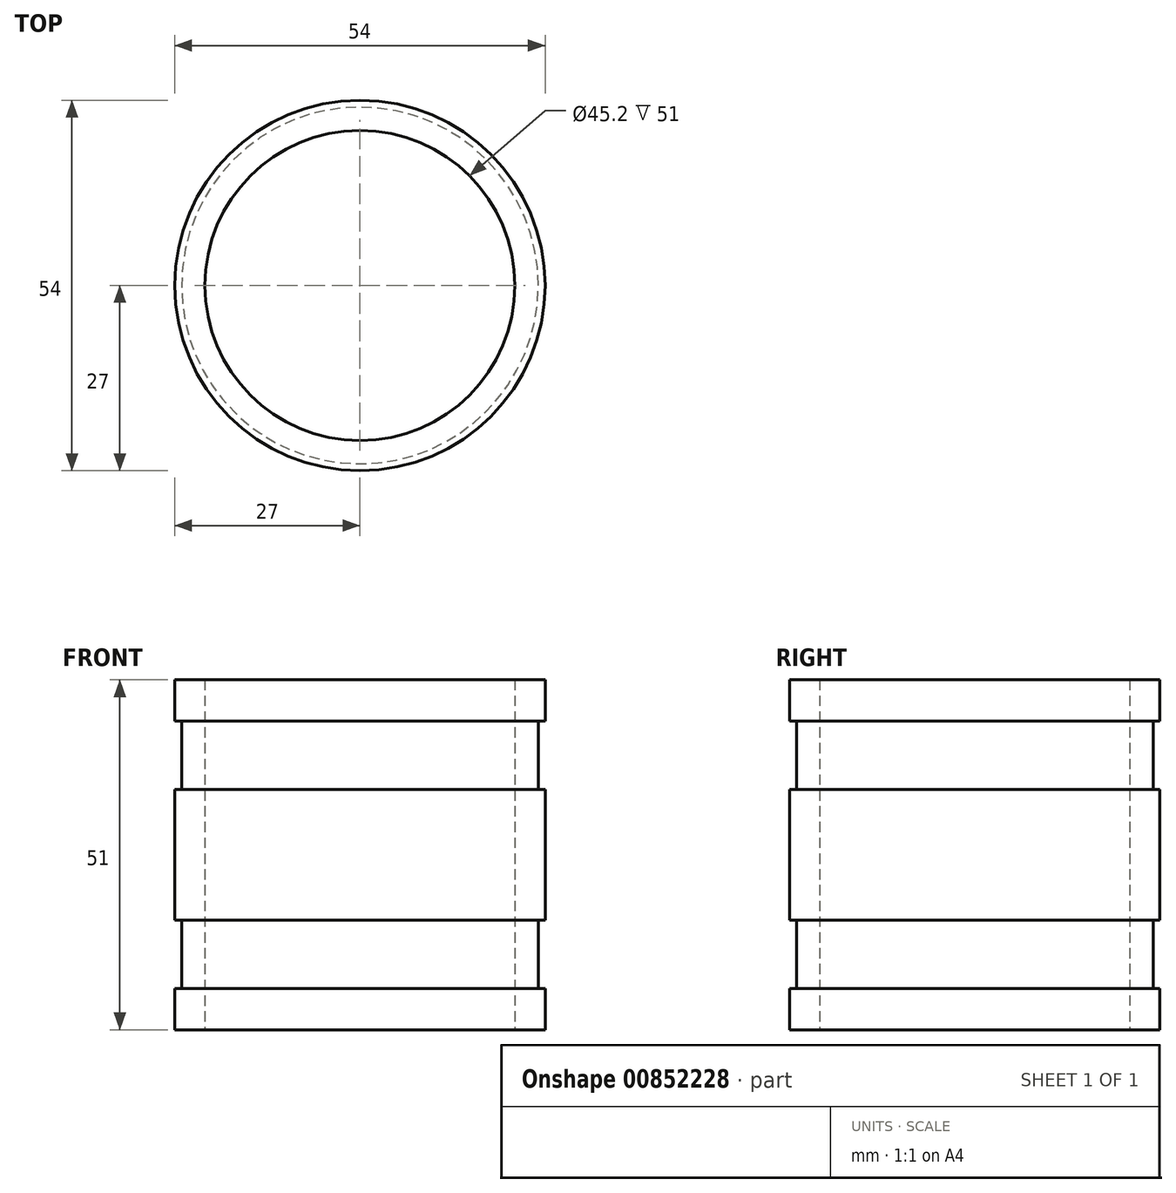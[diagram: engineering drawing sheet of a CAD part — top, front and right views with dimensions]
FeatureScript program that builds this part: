
annotation { "Feature Type Name" : "Feature", "Feature Type Description" : "" }
export const myFeature = defineFeature(function(context is Context, id is Id, definition is map)
    precondition{}
    {
        {
            var Q0;
            Q0=qCreatedBy(makeId("Top.planeOp"),FACE);
            var sketch = newSketch(context, id + "F0", { "sketchPlane" : qUnion([Q0])});
            skCircle(sketch, "E0", {"center": v(0, 0) * mm, "radius": 27 * mm});
            skSolve(sketch);
        }
        {
            var Q0;
            Q0=makeQuery(id+"F0.imprint","IMPRINT",FACE,{"disambiguationData":[TD([[makeQuery(id+"F0.imprint","IMPRINT",EDGE,{"derivedFrom":sQuery(id+"F0.wireOp",EDGE,"E0")}),1.0]])]});
            extrude(context, id + "F1", {"entities" : qUnion([Q0]), "depth" : 6 * mm, "offsetDistance" : 25 * mm});
        }
        {
            var Q0;
            Q0=makeQuery(id+"F1.opExtrude","CAP_FACE",FACE,{"disambiguationData":[OSD([sQuery(id+"F0.wireOp",EDGE,"E0")])],"isStart":false});
            var sketch = newSketch(context, id + "F2", { "sketchPlane" : qUnion([Q0])});
            skCircle(sketch, "E1", {"center": v(0, 0) * mm, "radius": 26 * mm});
            skSolve(sketch);
        }
        {
            var Q0;
            Q0=makeQuery(id+"F2.imprint","IMPRINT",FACE,{"disambiguationData":[TD([[makeQuery(id+"F2.imprint","IMPRINT",EDGE,{"derivedFrom":sQuery(id+"F2.wireOp",EDGE,"E1")}),1.0]])]});
            extrude(context, id + "F3", {"entities" : qUnion([Q0]), "operationType" : NewBodyOperationType.ADD, "depth" : 10 * mm, "offsetDistance" : 25 * mm});
        }
        {
            var Q0;
            Q0=makeQuery(id+"F3.opExtrude","CAP_FACE",FACE,{"disambiguationData":[OSD([sQuery(id+"F2.wireOp",EDGE,"E1")])],"isStart":false});
            var sketch = newSketch(context, id + "F4", { "sketchPlane" : qUnion([Q0])});
            skCircle(sketch, "E2", {"center": v(0, 0) * mm, "radius": 27 * mm});
            skSolve(sketch);
        }
        {
            var Q0;
            Q0 = qSketchRegion(id + "F4", true);
            extrude(context, id + "F5", {"entities" : qUnion([Q0]), "operationType" : NewBodyOperationType.ADD, "depth" : 19 * mm, "offsetDistance" : 25 * mm});
        }
        {
            var Q0;
            Q0=makeQuery(id+"F5.opExtrude","CAP_FACE",FACE,{"disambiguationData":[OSD([sQuery(id+"F4.wireOp",EDGE,"E2")])],"isStart":false});
            var sketch = newSketch(context, id + "F6", { "sketchPlane" : qUnion([Q0])});
            skCircle(sketch, "E3", {"center": v(0, 0) * mm, "radius": 26 * mm});
            skSolve(sketch);
        }
        {
            var Q0;
            Q0 = qSketchRegion(id + "F6", true);
            extrude(context, id + "F7", {"entities" : qUnion([Q0]), "operationType" : NewBodyOperationType.ADD, "depth" : 10 * mm, "offsetDistance" : 25 * mm});
        }
        {
            var Q0;
            Q0=makeQuery(id+"F7.opExtrude","CAP_FACE",FACE,{"disambiguationData":[OSD([sQuery(id+"F6.wireOp",EDGE,"E3")])],"isStart":false});
            var sketch = newSketch(context, id + "F8", { "sketchPlane" : qUnion([Q0])});
            skCircle(sketch, "E4", {"center": v(0, 0) * mm, "radius": 27 * mm});
            skSolve(sketch);
        }
        {
            var Q0;
            Q0 = qSketchRegion(id + "F8", true);
            extrude(context, id + "F9", {"entities" : qUnion([Q0]), "operationType" : NewBodyOperationType.ADD, "depth" : 6 * mm, "offsetDistance" : 25 * mm});
        }
        {
            var Q0;
            Q0=makeQuery(id+"F1.opExtrude","CAP_FACE",FACE,{"disambiguationData":[OSD([sQuery(id+"F0.wireOp",EDGE,"E0")])],"isStart":true});
            var sketch = newSketch(context, id + "F10", { "sketchPlane" : qUnion([Q0])});
            skCircle(sketch, "E5", {"center": v(0, 0) * mm, "radius": 22.6 * mm});
            skSolve(sketch);
        }
        {
            var Q0;
            Q0=makeQuery(id+"F10.imprint","IMPRINT",FACE,{"disambiguationData":[TD([[makeQuery(id+"F10.imprint","IMPRINT",EDGE,{"derivedFrom":sQuery(id+"F10.wireOp",EDGE,"E5")}),1.0]])]});
            extrude(context, id + "F11", {"entities" : qUnion([Q0]), "operationType" : NewBodyOperationType.REMOVE, "endBound" : BoundingType.THROUGH_ALL, "oppositeDirection" : true, "depth" : 25 * mm, "offsetDistance" : 25 * mm});
        }
    });
